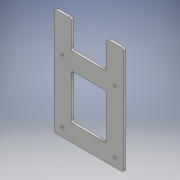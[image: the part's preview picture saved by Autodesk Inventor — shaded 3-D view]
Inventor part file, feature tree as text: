
AUTODESK INVENTOR PART (.ipt)
format: ipt  version: 2018 (Build 220112000, 112)  size: 146,432 bytes
history: native  units: mm
features: extrude x1, fillet x1, sketch x1
ambient origin geometry x8: Origin, YZ Plane, XZ Plane, XY Plane, X Axis, Y Axis, Z Axis, Center Point
bodies: Solid1 (feature_tree)
feature tree (3):
  extrude  "Extrusion1"  Depth=58.0mm
  fillet  "Fillet1"  Radius=2.7mm
  sketch  "Sketch1"  dims[d0=49.0mm d1=58.0mm d2=2.7mm d3=100.0mm d4=65.0mm d5=8.0mm d7=8.0mm d8=8.0mm d9=8.0mm d10=8.0mm d11=8.0mm d12=2.0mm d13=0.0mm d14=2.0mm d15=8.0mm]
